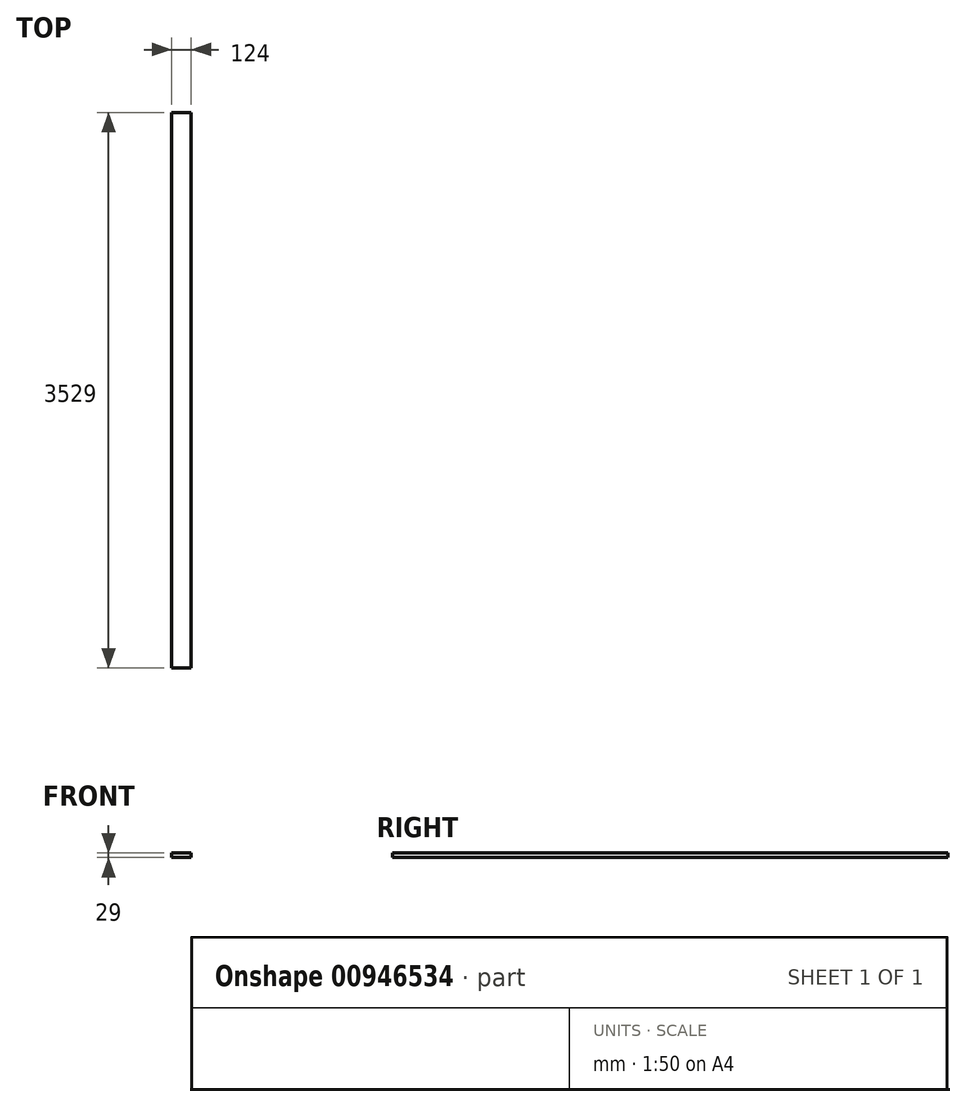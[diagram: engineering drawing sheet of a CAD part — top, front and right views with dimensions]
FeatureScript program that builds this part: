
annotation { "Feature Type Name" : "Feature", "Feature Type Description" : "" }
export const myFeature = defineFeature(function(context is Context, id is Id, definition is map)
    precondition{}
    {
        {
            var Q0;
            Q0=qCreatedBy(makeId("Front.planeOp"),FACE);
            var sketch = newSketch(context, id + "F0", { "sketchPlane" : qUnion([Q0])});
            skLineSegment(sketch, "E0.bottom", {"start": v(0, 0) * mm, "end": v(124, 0) * mm});
            skLineSegment(sketch, "E0.top", {"start": v(0, 29) * mm, "end": v(124, 29) * mm});
            skLineSegment(sketch, "E0.left", {"start": v(0, 0) * mm, "end": v(0, 29) * mm});
            skLineSegment(sketch, "E0.right", {"start": v(124, 0) * mm, "end": v(124, 29) * mm});
            skSolve(sketch);
        }
        {
            var Q0;
            Q0=qSketchRegion(id+"F0",true);
            extrude(context, id + "F1", {"entities" : qUnion([Q0]), "depth" : 3529 * mm, "offsetDistance" : 25 * mm});
        }
    });
